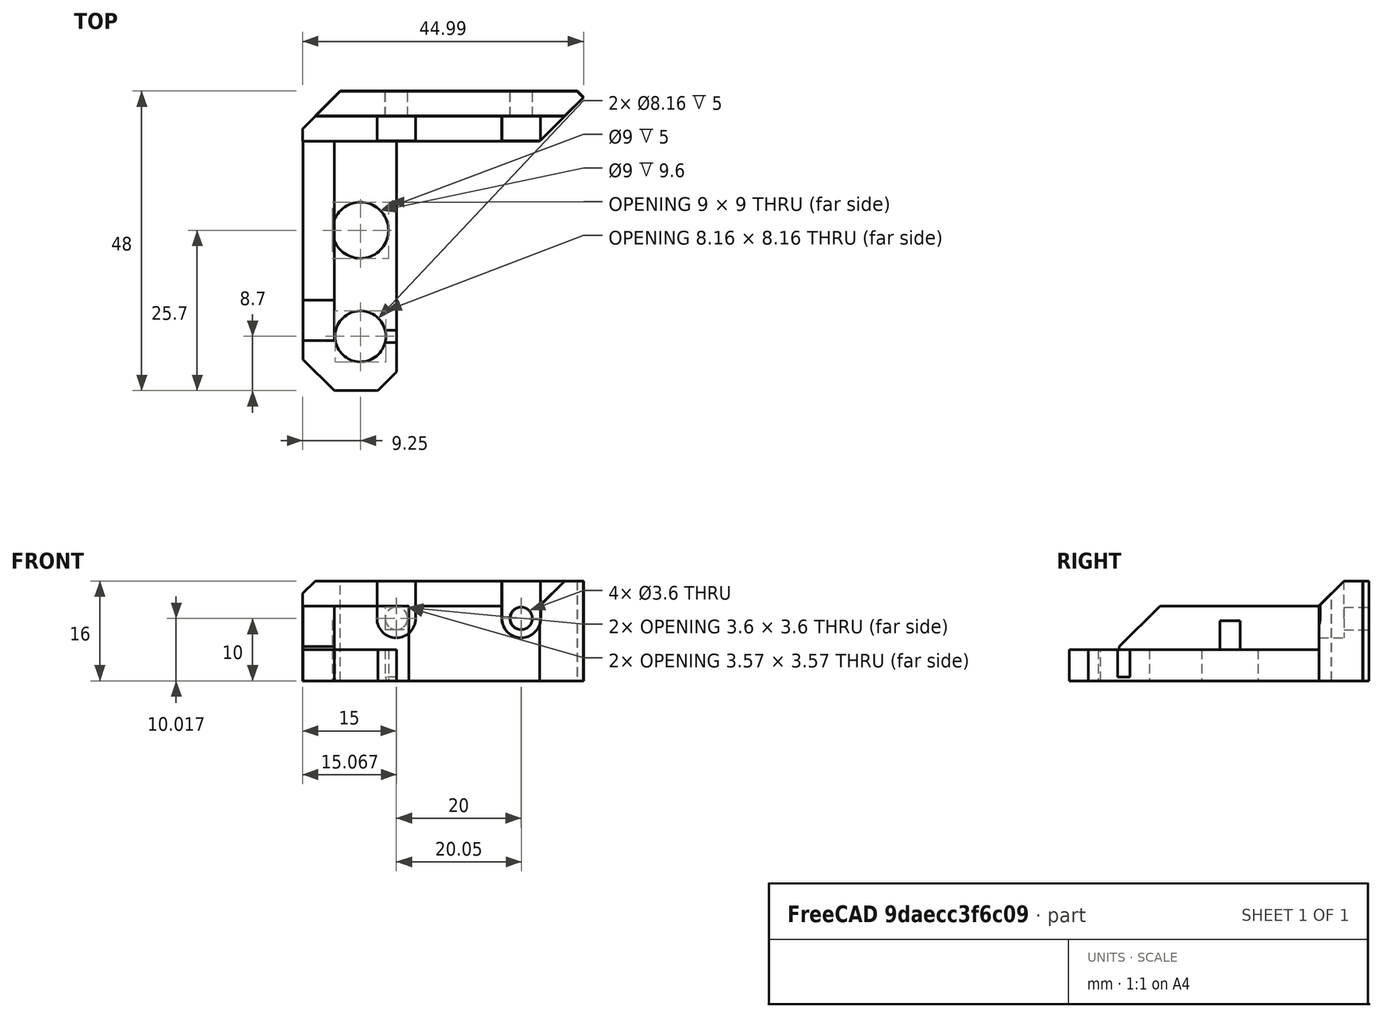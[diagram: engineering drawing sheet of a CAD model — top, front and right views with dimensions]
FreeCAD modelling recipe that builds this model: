
FCSTD DOCUMENT  (FreeCAD 0.14R3700 (Git))
Label: eje z izquierdo superior
License: CC-BY 3.0
LicenseURL: http://creativecommons.org/licenses/by/3.0/
objects: Part::MultiFuse×14, Part::Box×11, Part::Cut×9, Part::Cylinder×6, Part::Feature×5, Mesh::Feature×1, Part::Fuse×1
note: 46 computed .brp shape members not serialized (recipe doc carries the construction recipe); baked Part::Feature solids carry a one-line shape summary decoded from their .brp

FEATURE [Mesh::Feature] EJE_Z_izquierda_superior
FEATURE [Part::Feature] EJE_Z_izquierda_superior001
  shape: bbox 45 x 48 x 16 mm, 642 faces, 0 solids (baked)
FEATURE [Part::Feature] EJE_Z_izquierda_superior001_solid  label="EJE_Z_izquierda_superior001 (Solid)"
  shape: bbox 45 x 48 x 16 mm, 642 faces (baked)
FEATURE [Part::Feature] EJE_Z_izquierda_superior001_solid001  label="EJE_Z_izquierda_superior001 (Solid)001"
  Placement = pos=(41,-34,-200) rot=(0,0,1;0rad)
  shape: bbox 45 x 48 x 16 mm, 157 faces (baked)
FEATURE [Part::Box] Box  label="Cubo002"
  Height = 7
  Length = 5
  Placement = pos=(8.2,-19.7,10.5) rot=(1,0,0;0.785398rad)
  Width = 32
FEATURE [Part::Box] Box001  label="Cubo001"
  Height = 7
  Length = 5
  Placement = pos=(8.2,-19.7,10) rot=(0,0,1;0rad)
  Width = 32
FEATURE [Part::Cut] Cut
  Base = -> Box001
  Placement = pos=(-0.4,0,0) rot=(0,0,1;0rad)
  Tool = -> Box
FEATURE [Part::MultiFuse] Fusion
FEATURE [Part::Box] Box002  label="Cubo"
  Height = 5
  Length = 15
  Placement = pos=(-1.8,-27.7,5) rot=(0,0,1;0rad)
  Width = 40
FEATURE [Part::Cut] Cut001
  Base = -> Box002
  Placement = pos=(21,0,15) rot=(0,1,0;3.14159rad)
  Tool = -> Fusion
FEATURE [Part::Cylinder] Cylinder  label="Cilindro001"
  Angle = 360
  Height = 13
  Placement = pos=(4,-2,1) rot=(0,0,1;0rad)
  Radius = 4.5
FEATURE [Part::MultiFuse] Fusion002
  Shapes = -> [Cylinder]
FEATURE [Part::MultiFuse] Fusion001
  Placement = pos=(21,0,15.6) rot=(0,1,0;3.14159rad)
  Shapes = -> [Cylinder,Fusion002]
FEATURE [Part::Cut] Cut002
  Base = -> Cut001
  Tool = -> Fusion001
FEATURE [Part::MultiFuse] Fusion003
  Shapes = -> [Cut,Cut002]
FEATURE [Part::MultiFuse] Fusion004
  Shapes = -> [Box001,Box]
FEATURE [Part::Feature] EjeZ_soporte_superior  label="EjeZ_soporte_superior002"
  shape: bbox 38 x 93 x 16 mm, 307 faces, 0 solids (baked)
FEATURE [Part::Cut] Cut003
  Base = -> EjeZ_soporte_superior
  Placement = pos=(12.75,20.25,5) rot=(0,0,-1;1.5708rad)
  Tool = -> Fusion004
FEATURE [Part::Box] Box003  label="Cubo003"
  Height = 12
  Length = 17
  Placement = pos=(7.75,12.25,5) rot=(0,0,1;0rad)
  Width = 0.1
FEATURE [Part::Feature] Cut003_solid  label="Cut003 (Solid)"
  shape: bbox 45 x 8 x 16 mm, 122 faces (baked)
FEATURE [Part::Box] Box004  label="Cubo004"
  Height = 16
  Length = 45
  Placement = pos=(7.75,12.25,5) rot=(0,0,1;0rad)
  Width = 8
FEATURE [Part::Box] Box005  label="Cubo005"
  Height = 16
  Length = 45
  Placement = pos=(7.75,14.25,5) rot=(0,0,1;0.785398rad)
  Width = 8
FEATURE [Part::Box] Box006  label="Cubo006"
  Height = 16
  Length = 45
  Placement = pos=(29.75,42.2,5) rot=(0,0,-1;0.785398rad)
  Width = 8
FEATURE [Part::Box] Box007  label="Cubo007"
  Height = 16
  Length = 45
  Placement = pos=(39.75,-5,5) rot=(0,0,1;0.785398rad)
  Width = 8
FEATURE [Part::Box] Box008  label="Cubo008"
  Height = 16
  Length = 45
  Placement = pos=(7.75,4.25,20.31) rot=(-1,0,0;0.785398rad)
  Width = 8
FEATURE [Part::MultiFuse] Fusion005
  Shapes = -> [Box008,Box007,Box005,Box006]
FEATURE [Part::Cut] Cut004
  Base = -> Box004
  Tool = -> Fusion005
FEATURE [Part::Cylinder] Cylinder001  label="Cilindro"
  Angle = 360
  Height = 10
  Placement = pos=(22.75,12,15) rot=(-1,0,0;1.5708rad)
  Radius = 1.8
FEATURE [Part::Cylinder] Cylinder002  label="Cilindro002"
  Angle = 360
  Height = 4
  Placement = pos=(22.75,12.25,15) rot=(-1,0,0;1.5708rad)
  Radius = 3.1
FEATURE [Part::Box] Box009  label="Cubo009"
  Height = 8
  Length = 6.2
  Placement = pos=(19.65,12.25,15) rot=(0,0,1;0rad)
  Width = 4
FEATURE [Part::MultiFuse] Fusion006
  Shapes = -> [Cylinder001,Cylinder002,Box009]
FEATURE [Part::Box] Box010  label="Cubo010"
  Height = 8
  Length = 6.2
  Placement = pos=(19.65,12.25,15) rot=(0,0,1;0rad)
  Width = 4
FEATURE [Part::Cylinder] Cylinder003  label="Cilindro003"
  Angle = 360
  Height = 4
  Placement = pos=(22.75,12.25,15) rot=(-1,0,0;1.5708rad)
  Radius = 3.1
FEATURE [Part::Cylinder] Cylinder004  label="Cilindro004"
  Angle = 360
  Height = 10
  Placement = pos=(22.75,12,15) rot=(-1,0,0;1.5708rad)
  Radius = 1.8
FEATURE [Part::MultiFuse] Fusion007
  Placement = pos=(20,0,0) rot=(0,0,1;0rad)
  Shapes = -> [Cylinder004,Cylinder003,Box010]
FEATURE [Part::MultiFuse] Fusion008
  Shapes = -> [Fusion006,Fusion007]
FEATURE [Part::Cut] Cut005
  Base = -> Cut004
  Tool = -> Fusion008
FEATURE [Part::Fuse] Fusion009  label="EJE_Z_izquierda_superior002"
  Base = -> Fusion003
  Tool = -> Cut005
FEATURE [Part::Cylinder] Cylinder005  label="Cilindro005"
  Angle = 360
  Height = 13
  Placement = pos=(4,-2,1) rot=(0,0,1;0rad)
  Radius = 4.5
FEATURE [Part::MultiFuse] Fusion011
  Shapes = -> [Cylinder005]
FEATURE [Part::MultiFuse] Fusion010
  Placement = pos=(21,0,15.6) rot=(0,1,0;3.14159rad)
  Shapes = -> [Cylinder005,Fusion011]
FEATURE [Part::Cut] Cut006
  Base = -> Cut
  Tool = -> Fusion010
FEATURE [Part::MultiFuse] Fusion012
  Shapes = -> [Cut002,Cut006]
FEATURE [Part::MultiFuse] Fusion013
  Shapes = -> [Fusion006,Fusion007]
FEATURE [Part::Cut] Cut008
  Base = -> Box004
  Tool = -> Fusion005
FEATURE [Part::Cut] Cut007
  Base = -> Cut008
  Placement = pos=(0.05,0.05,0) rot=(0,0,1;0rad)
  Tool = -> Fusion013
FEATURE [Part::MultiFuse] Fusion014  label="EJE_Z_izquierda_superior003"
  Shapes = -> [Cut007,Fusion012]
